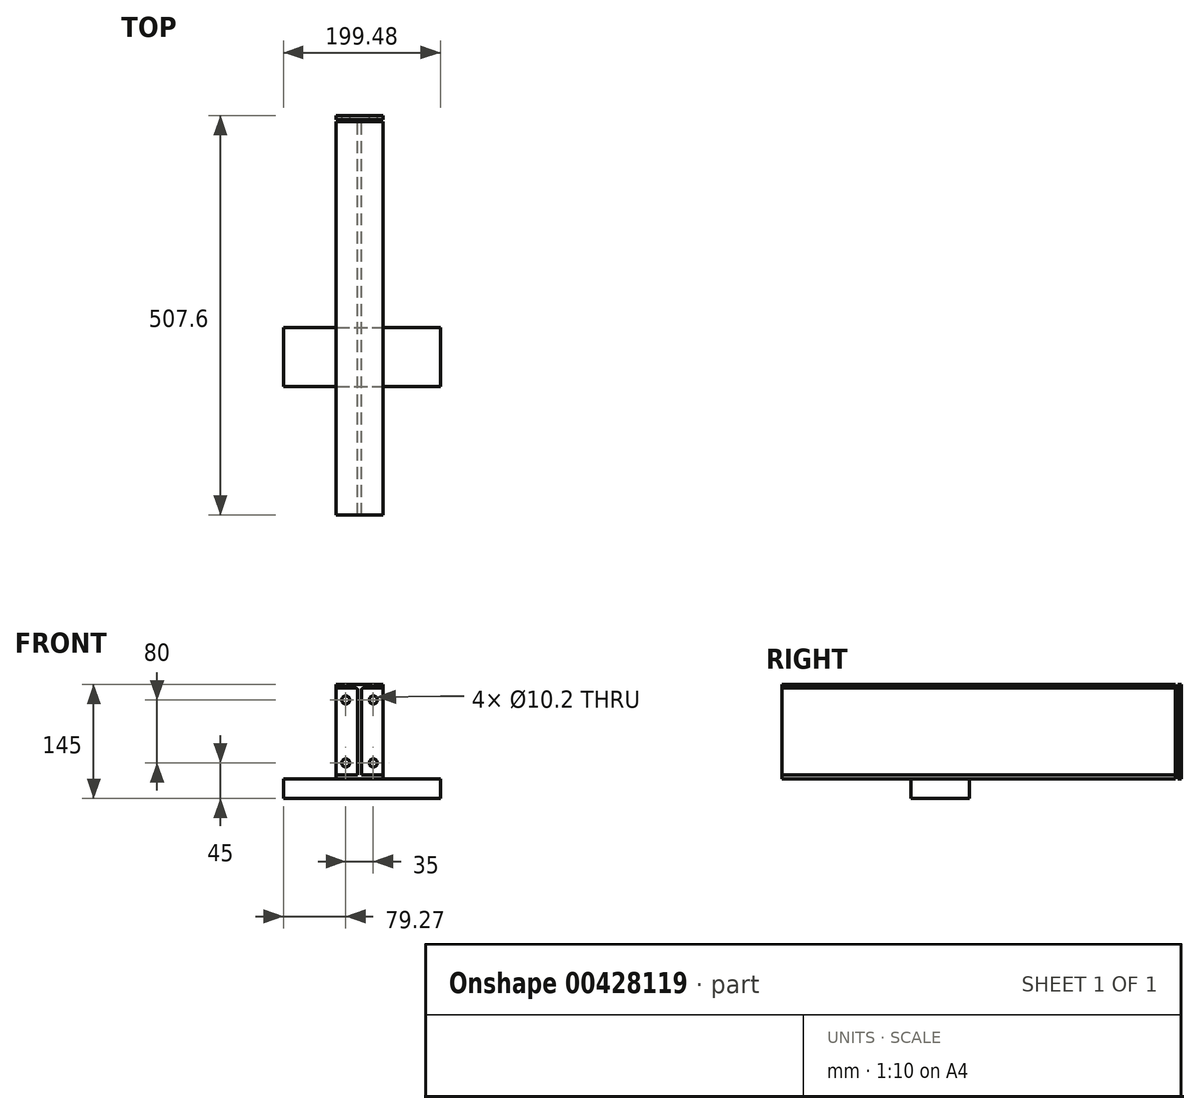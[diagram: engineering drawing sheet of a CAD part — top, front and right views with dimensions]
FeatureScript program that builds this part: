
annotation { "Feature Type Name" : "Feature", "Feature Type Description" : "" }
export const myFeature = defineFeature(function(context is Context, id is Id, definition is map)
    precondition{}
    {
        {
            var Q0;
            Q0=qCreatedBy(makeId("Front.planeOp"),FACE);
            var sketch = newSketch(context, id + "F0", { "sketchPlane" : qUnion([Q0])});
            skLineSegment(sketch, "E0", {"start": v(-2.5, 55) * mm, "end": v(-2.5, -55) * mm});
            skLineSegment(sketch, "E1", {"start": v(-2.5, -55) * mm, "end": v(-30, -55) * mm});
            skLineSegment(sketch, "E2", {"start": v(-30, -55) * mm, "end": v(-30, -60) * mm});
            skLineSegment(sketch, "E3", {"start": v(-30, -60) * mm, "end": v(30, -60) * mm});
            skLineSegment(sketch, "E4", {"start": v(30, -60) * mm, "end": v(30, -55) * mm});
            skLineSegment(sketch, "E5", {"start": v(30, -55) * mm, "end": v(2.5, -55) * mm});
            skLineSegment(sketch, "E6", {"start": v(2.5, -55) * mm, "end": v(2.5, 55) * mm});
            skLineSegment(sketch, "E7", {"start": v(2.5, 55) * mm, "end": v(30, 55) * mm});
            skLineSegment(sketch, "E8", {"start": v(30, 55) * mm, "end": v(30, 60) * mm});
            skLineSegment(sketch, "E9", {"start": v(30, 60) * mm, "end": v(-30, 60) * mm});
            skLineSegment(sketch, "E10", {"start": v(-30, 60) * mm, "end": v(-30, 55) * mm});
            skLineSegment(sketch, "E11", {"start": v(-30, 55) * mm, "end": v(-2.5, 55) * mm});
            skSolve(sketch);
        }
        {
            var Q0;
            Q0=makeQuery(id+"F0.imprint","IMPRINT",FACE,{"disambiguationData":[TD([[makeQuery(id+"F0.imprint","IMPRINT",EDGE,{"derivedFrom":sQuery(id+"F0.wireOp",EDGE,"E0")}),1.0]])]});
            extrude(context, id + "F1", {"entities" : qUnion([Q0]), "depth" : 500 * mm});
        }
        {
            var Q0;
            Q0=makeQuery(id+"F1.opExtrude","CAP_FACE",FACE,{"disambiguationData":[OSD([sQuery(id+"F0.wireOp",EDGE,"E0"),sQuery(id+"F0.wireOp",EDGE,"E1"),sQuery(id+"F0.wireOp",EDGE,"E2"),sQuery(id+"F0.wireOp",EDGE,"E3"),sQuery(id+"F0.wireOp",EDGE,"E4"),sQuery(id+"F0.wireOp",EDGE,"E5"),sQuery(id+"F0.wireOp",EDGE,"E6"),sQuery(id+"F0.wireOp",EDGE,"E7"),sQuery(id+"F0.wireOp",EDGE,"E8"),sQuery(id+"F0.wireOp",EDGE,"E9"),sQuery(id+"F0.wireOp",EDGE,"E10"),sQuery(id+"F0.wireOp",EDGE,"E11")])],"isStart":true});
            cPlane(context, id + "F2", {"entities" : qUnion([Q0]), "cplaneType" : CPlaneType.OFFSET, "offset" : 2.6 * mm, "width" : 150 * mm, "height" : 150 * mm});
        }
        {
            var Q0;
            Q0=qCreatedBy(id+"F2.planeOp",FACE);
            var sketch = newSketch(context, id + "F3", { "sketchPlane" : qUnion([Q0])});
            skLineSegment(sketch, "E12.bottom", {"start": v(-30, 60) * mm, "end": v(30, 60) * mm});
            skLineSegment(sketch, "E12.top", {"start": v(-30, -60) * mm, "end": v(30, -60) * mm});
            skLineSegment(sketch, "E12.left", {"start": v(-30, 60) * mm, "end": v(-30, -60) * mm});
            skLineSegment(sketch, "E12.right", {"start": v(30, 60) * mm, "end": v(30, -60) * mm});
            skCircle(sketch, "E13", {"center": v(-17.5, 40) * mm, "radius": 5.1 * mm});
            skCircle(sketch, "E14", {"center": v(17.5, 40) * mm, "radius": 5.1 * mm});
            skCircle(sketch, "E15", {"center": v(-17.5, -40) * mm, "radius": 5.1 * mm});
            skCircle(sketch, "E16", {"center": v(17.5, -40) * mm, "radius": 5.1 * mm});
            skSolve(sketch);
        }
        {
            var Q0;
            Q0 = qSketchRegion(id + "F3", true);
            extrude(context, id + "F4", {"entities" : qUnion([Q0]), "depth" : 5 * mm});
        }
        {
            var Q0;
            Q0=makeQuery(id+"F1.opExtrude","SWEPT_EDGE",EDGE,{"disambiguationData":[OSD([sQuery(id+"F0.wireOp",EDGE,"E6"),sQuery(id+"F0.wireOp",EDGE,"E7")])]});
            fillet(context, id + "F5", {"entities" : qUnion([Q0]), "radius" : 2 * mm, "tangentPropagation" : true, "allowEdgeOverflow" : false});
        }
        {
            var Q0;
            Q0=makeQuery(id+"F1.opExtrude","SWEPT_EDGE",EDGE,{"disambiguationData":[OSD([sQuery(id+"F0.wireOp",EDGE,"E0"),sQuery(id+"F0.wireOp",EDGE,"E11")])]});
            fillet(context, id + "F6", {"entities" : qUnion([Q0]), "radius" : 2 * mm, "tangentPropagation" : true, "allowEdgeOverflow" : false});
        }
        {
            var Q0;
            Q0=makeQuery(id+"F1.opExtrude","SWEPT_FACE",FACE,{"disambiguationData":[OSD([sQuery(id+"F0.wireOp",EDGE,"E3")])]});
            var sketch = newSketch(context, id + "F7", { "sketchPlane" : qUnion([Q0])});
            skLineSegment(sketch, "E17.bottom", {"start": v(-96.77, 261.83) * mm, "end": v(102.71, 261.83) * mm});
            skLineSegment(sketch, "E17.top", {"start": v(-96.77, 336.55) * mm, "end": v(102.71, 336.55) * mm});
            skLineSegment(sketch, "E17.left", {"start": v(-96.77, 261.83) * mm, "end": v(-96.77, 336.55) * mm});
            skLineSegment(sketch, "E17.right", {"start": v(102.71, 261.83) * mm, "end": v(102.71, 336.55) * mm});
            skSolve(sketch);
        }
        {
            var Q0;
            Q0 = qSketchRegion(id + "F7", true);
            extrude(context, id + "F8", {"entities" : qUnion([Q0]), "depth" : 25 * mm});
        }
    });
